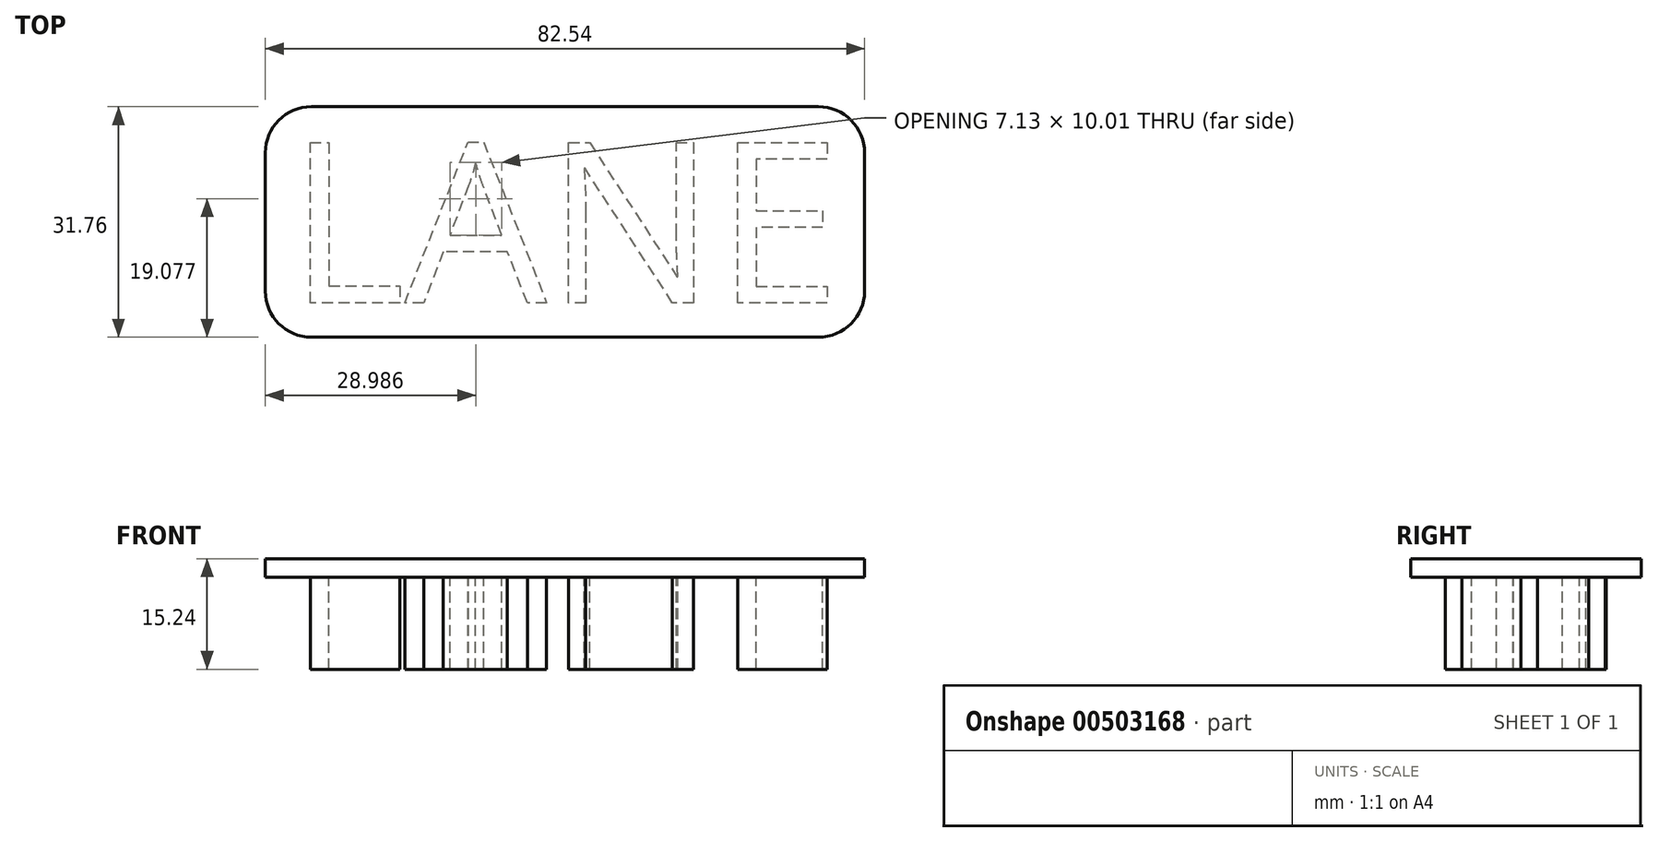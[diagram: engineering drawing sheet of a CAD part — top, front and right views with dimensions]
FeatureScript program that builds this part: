
annotation { "Feature Type Name" : "Feature", "Feature Type Description" : "" }
export const myFeature = defineFeature(function(context is Context, id is Id, definition is map)
    precondition{}
    {
        {
            var Q0;
            Q0=qCreatedBy(makeId("Top.planeOp"),FACE);
            var sketch = newSketch(context, id + "F0", { "sketchPlane" : qUnion([Q0])});
            skText(sketch, "E0", { "text": "LANE", "fontName": "OpenSans-Regular.ttf"});
            const initialGuessF0  = {"E0": [-0.0381, -0.01113, 1, 0, 0.02224]};
            skSetInitialGuess(sketch, initialGuessF0);
            skSolve(sketch);
        }
        {
            var Q0;
            Q0 = qSketchRegion(id + "F0", true);
            extrude(context, id + "F1", {"entities" : qUnion([Q0]), "oppositeDirection" : true, "depth" : 12.7 * mm});
        }
        {
            var Q0;
            Q0=qCreatedBy(makeId("Top.planeOp"),FACE);
            var sketch = newSketch(context, id + "F2", { "sketchPlane" : qUnion([Q0])});
            skLineSegment(sketch, "E1.bottom", {"start": v(41.28, 15.88) * mm, "end": v(-41.28, 15.88) * mm});
            skLineSegment(sketch, "E1.top", {"start": v(41.28, -15.88) * mm, "end": v(-41.28, -15.88) * mm});
            skLineSegment(sketch, "E1.left", {"start": v(41.28, 15.88) * mm, "end": v(41.28, -15.88) * mm});
            skLineSegment(sketch, "E1.right", {"start": v(-41.28, 15.88) * mm, "end": v(-41.28, -15.88) * mm});
            skPoint(sketch, "E1.middle", {"position": v(0, 0) * mm});
            skSolve(sketch);
        }
        {
            var Q0;
            Q0=makeQuery(id+"F2.imprint","IMPRINT",FACE,{"disambiguationData":[TD([[makeQuery(id+"F2.imprint","IMPRINT",EDGE,{"derivedFrom":sQuery(id+"F2.wireOp",EDGE,"E1.bottom")}),1.0]])]});
            extrude(context, id + "F3", {"entities" : qUnion([Q0]), "depth" : 2.54 * mm});
        }
        {
            var Q0;
            Q0=makeQuery(id+"F3.opExtrude","SWEPT_EDGE",EDGE,{"disambiguationData":[OSD([sQuery(id+"F2.wireOp",EDGE,"E1.bottom"),sQuery(id+"F2.wireOp",EDGE,"E1.right")])]});
            var Q1;
            Q1=makeQuery(id+"F3.opExtrude","SWEPT_EDGE",EDGE,{"disambiguationData":[OSD([sQuery(id+"F2.wireOp",EDGE,"E1.top"),sQuery(id+"F2.wireOp",EDGE,"E1.right")])]});
            var Q2;
            Q2=makeQuery(id+"F3.opExtrude","SWEPT_EDGE",EDGE,{"disambiguationData":[OSD([sQuery(id+"F2.wireOp",EDGE,"E1.top"),sQuery(id+"F2.wireOp",EDGE,"E1.left")])]});
            var Q3;
            Q3=makeQuery(id+"F3.opExtrude","SWEPT_EDGE",EDGE,{"disambiguationData":[OSD([sQuery(id+"F2.wireOp",EDGE,"E1.bottom"),sQuery(id+"F2.wireOp",EDGE,"E1.left")])]});
            fillet(context, id + "F4", {"entities" : qUnion([Q0, Q1, Q2, Q3]), "radius" : 6.35 * mm, "tangentPropagation" : true, "allowEdgeOverflow" : false});
        }
    });
